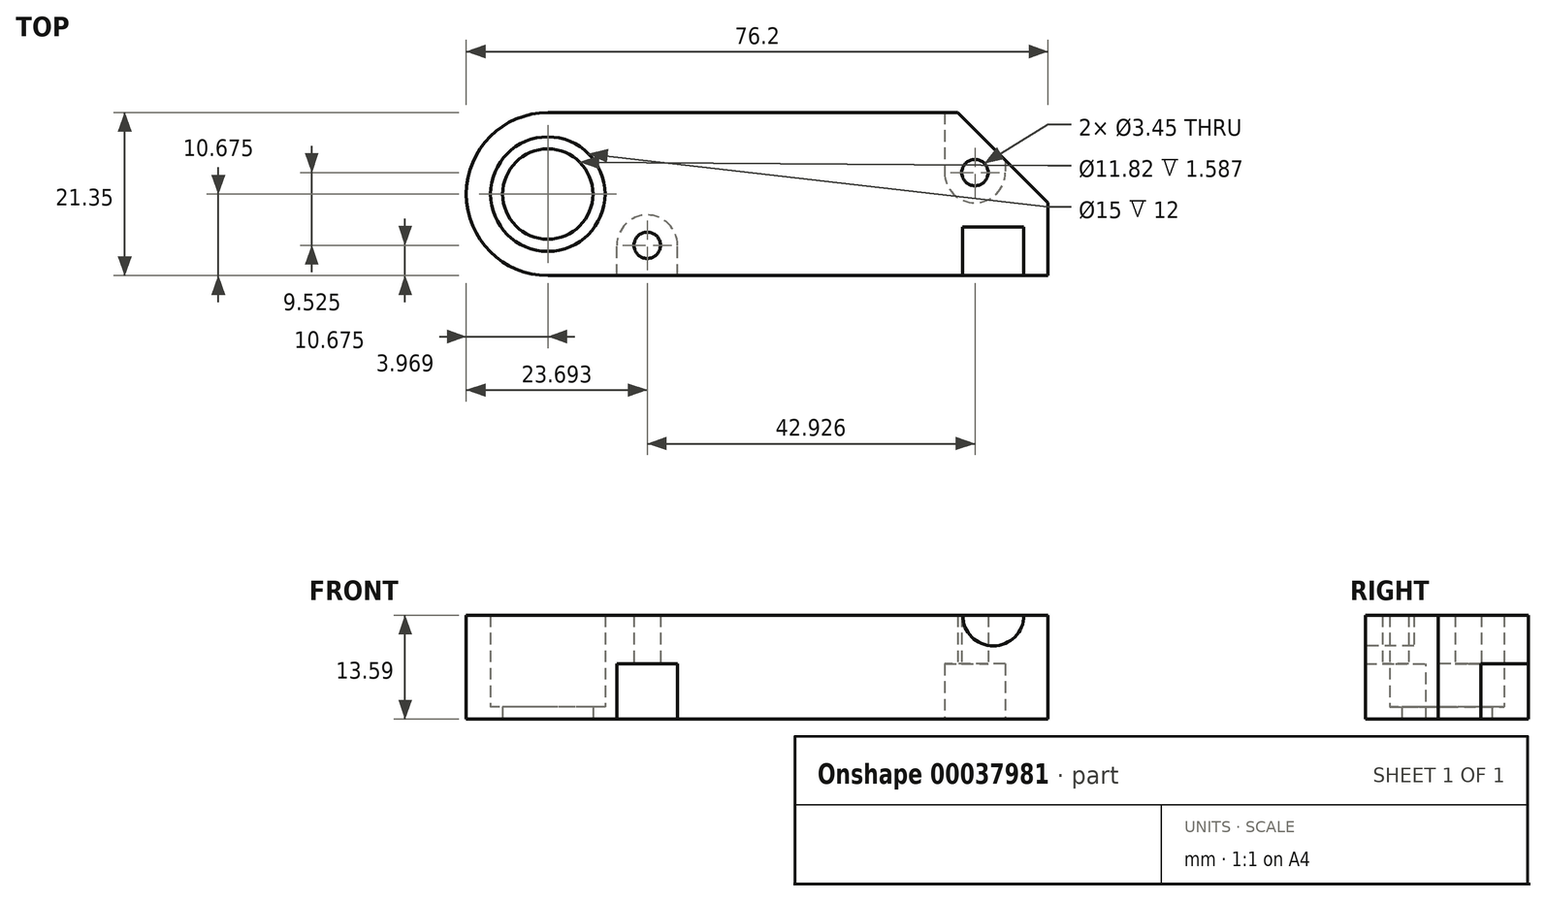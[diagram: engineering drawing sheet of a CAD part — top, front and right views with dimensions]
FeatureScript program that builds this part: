
annotation { "Feature Type Name" : "Feature", "Feature Type Description" : "" }
export const myFeature = defineFeature(function(context is Context, id is Id, definition is map)
    precondition{}
    {
        {
            var Q0;
            Q0=qCreatedBy(makeId("Top.planeOp"),FACE);
            var sketch = newSketch(context, id + "F0", { "sketchPlane" : qUnion([Q0])});
            skLineSegment(sketch, "E0.bottom", {"start": v(0, 0) * mm, "end": v(64.38, 0) * mm});
            skLineSegment(sketch, "E0.top", {"start": v(0, -21.35) * mm, "end": v(76.2, -21.35) * mm});
            skCircle(sketch, "E1", {"center": v(10.67, -10.67) * mm, "radius": 10.67 * mm, "construction": true});
            skLineSegment(sketch, "E2", {"start": v(0, 0) * mm, "end": v(0, -21.35) * mm});
            skLineSegment(sketch, "E3", {"start": v(76.2, -21.35) * mm, "end": v(76.2, -11.82) * mm});
            skLineSegment(sketch, "E4", {"start": v(76.2, -11.82) * mm, "end": v(64.38, 0) * mm});
            skCircle(sketch, "E5", {"center": v(10.67, -10.67) * mm, "radius": 5.91 * mm});
            skLineSegment(sketch, "E6", {"start": v(76.2, -11.82) * mm, "end": v(61.85, -11.82) * mm, "construction": true});
            skLineSegment(sketch, "E7", {"start": v(61.85, -11.82) * mm, "end": v(61.85, -21.35) * mm, "construction": true});
            skCircle(sketch, "E8", {"center": v(23.7, -17.38) * mm, "radius": 3.97 * mm, "construction": true});
            skCircle(sketch, "E9", {"center": v(66.62, -7.86) * mm, "radius": 3.97 * mm, "construction": true});
            skCircle(sketch, "E10", {"center": v(23.7, -17.38) * mm, "radius": 1.73 * mm});
            skCircle(sketch, "E11", {"center": v(66.62, -7.86) * mm, "radius": 1.73 * mm});
            skSolve(sketch);
        }
        {
            var Q0;
            Q0 = qSketchRegion(id + "F0", true);
            extrude(context, id + "F1", {"entities" : qUnion([Q0]), "depth" : 1.59 * mm});
        }
        {
            var Q0;
            Q0=makeQuery(id+"F1.opExtrude","CAP_FACE",FACE,{"disambiguationData":[OSD([sQuery(id+"F0.wireOp",EDGE,"E0.bottom"),sQuery(id+"F0.wireOp",EDGE,"E0.top"),sQuery(id+"F0.wireOp",EDGE,"E2"),sQuery(id+"F0.wireOp",EDGE,"E3"),sQuery(id+"F0.wireOp",EDGE,"E4"),sQuery(id+"F0.wireOp",EDGE,"E5"),sQuery(id+"F0.wireOp",EDGE,"E10"),sQuery(id+"F0.wireOp",EDGE,"E11")])],"isStart":false});
            var sketch = newSketch(context, id + "F2", { "sketchPlane" : qUnion([Q0])});
            skCircle(sketch, "E12", {"center": v(10.67, -10.67) * mm, "radius": 7.5 * mm});
            skSolve(sketch);
        }
        {
            var Q0;
            Q0=makeQuery(id+"F2.imprint","IMPRINT",FACE,{"disambiguationData":[TD([[makeQuery(id+"F2.imprint","IMPRINT",EDGE,{"derivedFrom":sQuery(id+"F2.wireOp",EDGE,"E12")}),-1.0]])]});
            extrude(context, id + "F3", {"entities" : qUnion([Q0]), "operationType" : NewBodyOperationType.ADD, "depth" : 12 * mm});
        }
        {
            var Q0;
            {var subQ0=sQuery(id+"F0.wireOp",EDGE,"E0.top");Q0=makeQuery(id+"F3.boolean.opBoolean","MERGE",FACE,{"derivedFrom":[makeQuery(id+"F1.opExtrude","SWEPT_FACE",FACE,{"disambiguationData":[OSD([subQ0])]}),makeQuery(id+"F3.opExtrude","SWEPT_FACE",FACE,{"disambiguationData":[OSD([subQ0])]})]});}
            var sketch = newSketch(context, id + "F4", { "sketchPlane" : qUnion([Q0])});
            skArc(sketch, "E13", {"start": v(65.03, 13.59) * mm, "mid": v(69.03, 9.59) * mm, "end": v(73.03, 13.59) * mm});
            skLineSegment(sketch, "E14", {"start": v(65.03, 13.59) * mm, "end": v(73.03, 13.59) * mm});
            skSolve(sketch);
        }
        {
            var Q0;
            Q0 = qSketchRegion(id + "F4", true);
            extrude(context, id + "F5", {"entities" : qUnion([Q0]), "operationType" : NewBodyOperationType.REMOVE, "oppositeDirection" : true, "depth" : 6.35 * mm});
        }
        {
            var Q0;
            {var subQ0=sQuery(id+"F0.wireOp",EDGE,"E2");var subQ1=sQuery(id+"F0.wireOp",EDGE,"E0.top");Q0=makeQuery(id+"F3.boolean.opBoolean","MERGE",EDGE,{"derivedFrom":[makeQuery(id+"F1.opExtrude","SWEPT_EDGE",EDGE,{"disambiguationData":[OSD([subQ1,subQ0])]}),makeQuery(id+"F3.opExtrude","SWEPT_EDGE",EDGE,{"disambiguationData":[OSD([subQ1,subQ0])]})]});}
            var Q1;
            {var subQ0=sQuery(id+"F0.wireOp",EDGE,"E2");var subQ1=sQuery(id+"F0.wireOp",EDGE,"E0.bottom");Q1=makeQuery(id+"F3.boolean.opBoolean","MERGE",EDGE,{"derivedFrom":[makeQuery(id+"F1.opExtrude","SWEPT_EDGE",EDGE,{"disambiguationData":[OSD([subQ1,subQ0])]}),makeQuery(id+"F3.opExtrude","SWEPT_EDGE",EDGE,{"disambiguationData":[OSD([subQ1,subQ0])]})]});}
            fillet(context, id + "F6", {"entities" : qUnion([Q0, Q1]), "radius" : 10.67 * mm, "tangentPropagation" : true, "allowEdgeOverflow" : false});
        }
        {
            var Q0;
            Q0=makeQuery(id+"F1.opExtrude","CAP_FACE",FACE,{"disambiguationData":[OSD([sQuery(id+"F0.wireOp",EDGE,"E0.bottom"),sQuery(id+"F0.wireOp",EDGE,"E0.top"),sQuery(id+"F0.wireOp",EDGE,"E2"),sQuery(id+"F0.wireOp",EDGE,"E3"),sQuery(id+"F0.wireOp",EDGE,"E4"),sQuery(id+"F0.wireOp",EDGE,"E5"),sQuery(id+"F0.wireOp",EDGE,"E10"),sQuery(id+"F0.wireOp",EDGE,"E11")])],"isStart":true});
            var sketch = newSketch(context, id + "F7", { "sketchPlane" : qUnion([Q0])});
            skLineSegment(sketch, "E15.rect.bottom", {"start": v(19.72, 21.35) * mm, "end": v(27.66, 21.35) * mm});
            skLineSegment(sketch, "E15.rect.top", {"start": v(19.72, 13.41) * mm, "end": v(27.66, 13.41) * mm});
            skLineSegment(sketch, "E15.rect.left", {"start": v(19.72, 21.35) * mm, "end": v(19.72, 13.41) * mm});
            skLineSegment(sketch, "E15.rect.right", {"start": v(27.66, 21.35) * mm, "end": v(27.66, 13.41) * mm});
            skPoint(sketch, "E15.rect.middle", {"position": v(23.7, 17.38) * mm});
            skLineSegment(sketch, "E16.bottom", {"start": v(62.65, 0) * mm, "end": v(64.38, 0) * mm});
            skLineSegment(sketch, "E16.top", {"start": v(62.65, 11.82) * mm, "end": v(70.59, 11.82) * mm});
            skLineSegment(sketch, "E16.left", {"start": v(62.65, 0) * mm, "end": v(62.65, 11.82) * mm});
            skLineSegment(sketch, "E16.right", {"start": v(70.59, 6.21) * mm, "end": v(70.59, 11.82) * mm});
            skLineSegment(sketch, "E17", {"start": v(66.62, 7.86) * mm, "end": v(66.62, 15.8) * mm, "construction": true});
            skPoint(sketch, "E18", {"position": v(66.62, 11.82) * mm});
            skLineSegment(sketch, "E19", {"start": v(64.38, 0) * mm, "end": v(70.59, 6.21) * mm});
            skSolve(sketch);
        }
        {
            var Q0;
            Q0 = qSketchRegion(id + "F7", true);
            extrude(context, id + "F8", {"entities" : qUnion([Q0]), "operationType" : NewBodyOperationType.REMOVE, "oppositeDirection" : true, "depth" : 7.24 * mm});
        }
        {
            var Q0;
            Q0=makeQuery(id+"F8.boolean.opBoolean","COPY",EDGE,{"derivedFrom":makeQuery(id+"F8.opExtrude","SWEPT_EDGE",EDGE,{"disambiguationData":[OSD([sQuery(id+"F7.wireOp",EDGE,"E16.top"),sQuery(id+"F7.wireOp",EDGE,"E16.left")])]})});
            var Q1;
            Q1=makeQuery(id+"F8.boolean.opBoolean","COPY",EDGE,{"derivedFrom":makeQuery(id+"F8.opExtrude","SWEPT_EDGE",EDGE,{"disambiguationData":[OSD([sQuery(id+"F7.wireOp",EDGE,"E16.top"),sQuery(id+"F7.wireOp",EDGE,"E16.right")])]})});
            var Q2;
            Q2=makeQuery(id+"F8.boolean.opBoolean","COPY",EDGE,{"derivedFrom":makeQuery(id+"F8.opExtrude","SWEPT_EDGE",EDGE,{"disambiguationData":[OSD([sQuery(id+"F7.wireOp",EDGE,"E15.rect.top"),sQuery(id+"F7.wireOp",EDGE,"E15.rect.left")])]})});
            var Q3;
            Q3=makeQuery(id+"F8.boolean.opBoolean","COPY",EDGE,{"derivedFrom":makeQuery(id+"F8.opExtrude","SWEPT_EDGE",EDGE,{"disambiguationData":[OSD([sQuery(id+"F7.wireOp",EDGE,"E15.rect.top"),sQuery(id+"F7.wireOp",EDGE,"E15.rect.right")])]})});
            fillet(context, id + "F9", {"entities" : qUnion([Q0, Q1, Q2, Q3]), "radius" : 3.97 * mm, "tangentPropagation" : true, "allowEdgeOverflow" : false});
        }
    });
